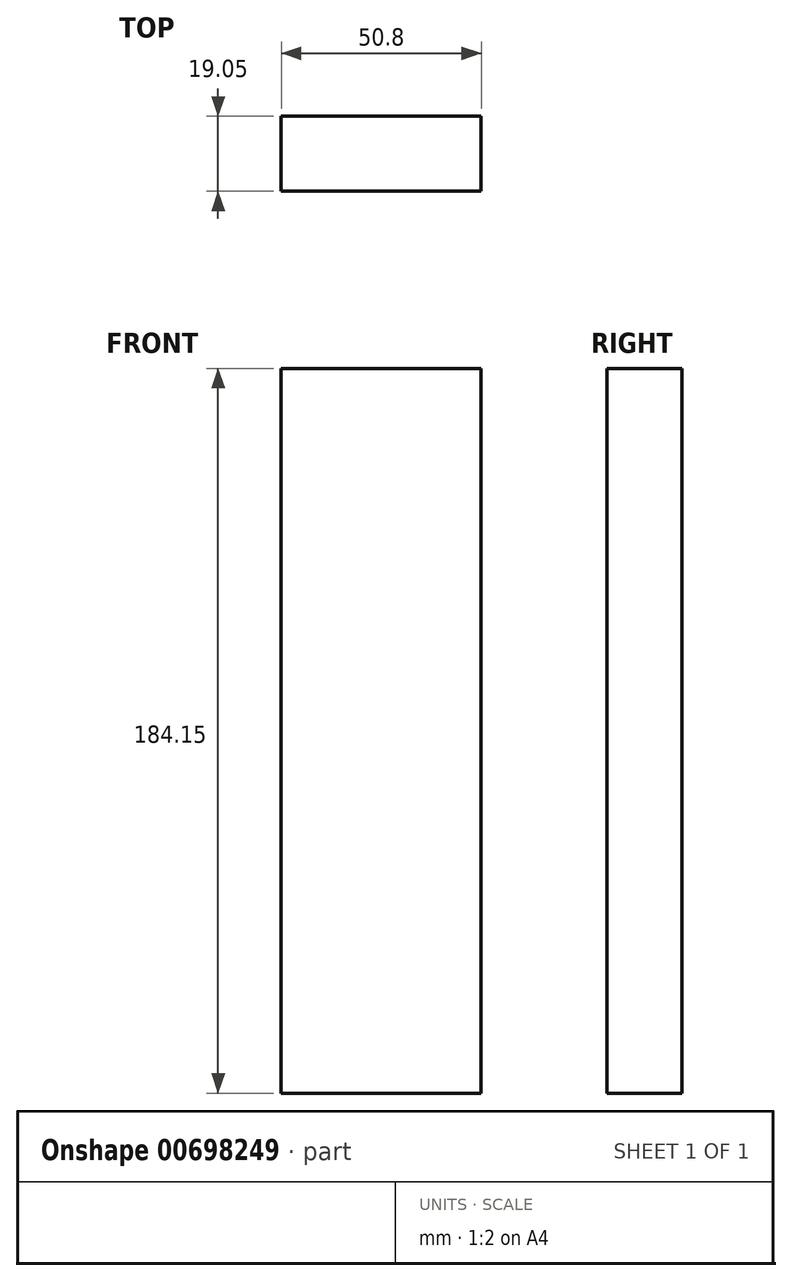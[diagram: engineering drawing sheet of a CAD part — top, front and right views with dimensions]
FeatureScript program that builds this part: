
annotation { "Feature Type Name" : "Feature", "Feature Type Description" : "" }
export const myFeature = defineFeature(function(context is Context, id is Id, definition is map)
    precondition{}
    {
        {
            var Q0;
            Q0=qCreatedBy(makeId("Front.planeOp"),FACE);
            var sketch = newSketch(context, id + "F0", { "sketchPlane" : qUnion([Q0])});
            skLineSegment(sketch, "E0.bottom", {"start": v(-3.11, -180.6) * mm, "end": v(-53.91, -180.6) * mm});
            skLineSegment(sketch, "E0.top", {"start": v(-3.11, 3.54) * mm, "end": v(-53.91, 3.54) * mm});
            skLineSegment(sketch, "E0.left", {"start": v(-3.11, -180.6) * mm, "end": v(-3.11, 3.54) * mm});
            skLineSegment(sketch, "E0.right", {"start": v(-53.91, -180.6) * mm, "end": v(-53.91, 3.54) * mm});
            skSolve(sketch);
        }
        {
            var Q0;
            Q0 = qSketchRegion(id + "F0", true);
            extrude(context, id + "F1", {"entities" : qUnion([Q0]), "depth" : 19.05 * mm, "offsetDistance" : 25.4 * mm});
        }
    });
